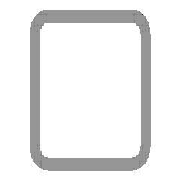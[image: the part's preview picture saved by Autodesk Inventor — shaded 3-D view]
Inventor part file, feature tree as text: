
AUTODESK INVENTOR PART (.ipt)
format: ipt  version: 2022 (Build 260153000, 153)  size: 264,192 bytes
history: native  units: mm (DEFAULTED — no unit token found)
features: other x7, sketch x3, surface_op x2, plane x1
ambient origin geometry x8: Origin, YZ Plane, XZ Plane, XY Plane, X Axis, Y Axis, Z Axis, Center Point
bodies: Solid1 (feature_tree), Body (feature_tree), Solid3 (feature_tree)
feature tree (13):
  parser-record x1  (decoder bookkeeping rows leaked as tree rows — omitted from the tree; the rows remain in map.json)
  other  "Driven Length"
  other  "Start Plane"
  other  "End Plane"
  sketch  "Sketch"  dims[d7=6.0mm d10=40.0mm d11=40.0mm d12=4.0mm d13=-0.0mm d14=180.0mm d15=20.0mm d16=20.0mm d17=90.0deg d18=180.0mm d37=5.0mm d38=5.0mm d39=5.0mm d40=5.0mm d41=5.0mm d42=5.0mm d43=5.0mm d44=5.0mm d45=0.0mm d46=5.0mm d47=5.0mm d48=5.0mm d49=5.0mm d50=5.0mm d51=5.0mm d52=5.0mm d53=5.0mm d54=0.0mm]
  sketch  "Sketch3"  dims[d3=155.0mm]
  plane  "Work Plane3"
  sketch  "Sketch4"  dims[d4=0.0mm]
  other  "Srf5"
  other  "Srf6"
  other  "Srf4"
  surface_op  "Boundary Patch3"
  surface_op  "Boundary Patch4"
